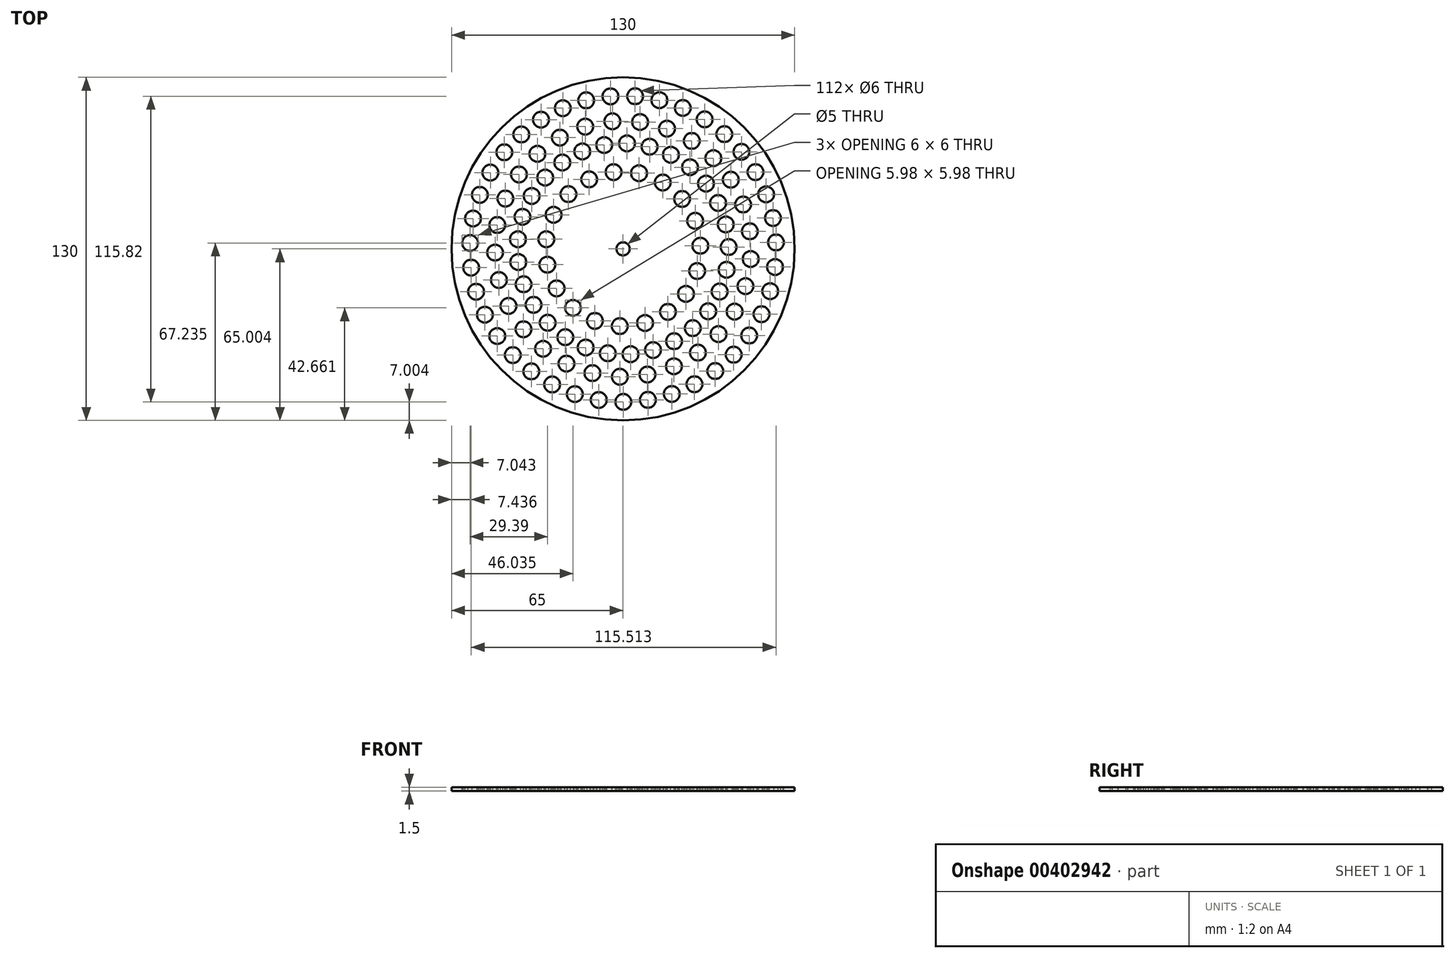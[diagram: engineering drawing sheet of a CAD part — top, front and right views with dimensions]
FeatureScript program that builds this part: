
annotation { "Feature Type Name" : "Feature", "Feature Type Description" : "" }
export const myFeature = defineFeature(function(context is Context, id is Id, definition is map)
    precondition{}
    {
        {
            var Q0;
            Q0=qCreatedBy(makeId("Top.planeOp"),FACE);
            var sketch = newSketch(context, id + "F0", { "sketchPlane" : qUnion([Q0])});
            skCircle(sketch, "E0", {"center": v(-32.16, 21.23) * mm, "radius": 65 * mm});
            skCircle(sketch, "E1", {"center": v(-32.16, 21.23) * mm, "radius": 2.5 * mm});
            skSolve(sketch);
        }
        {
            var Q0;
            Q0 = qSketchRegion(id + "F0", true);
            extrude(context, id + "F1", {"entities" : qUnion([Q0]), "flatOperationType" : FlatOperationType.REMOVE, "offsetDistance" : 25 * mm, "depth" : 1.5 * mm, "domain" : OperationDomain.MODEL});
        }
        {
            var Q0;
            Q0=makeQuery(id+"F1.opExtrude","CAP_FACE",FACE,{"disambiguationData":[OSD([sQuery(id+"F0.wireOp",EDGE,"E0")])],"isStart":false});
            var sketch = newSketch(context, id + "F2", { "sketchPlane" : qUnion([Q0])});
            skCircle(sketch, "E2", {"center": v(-90.12, 23.46) * mm, "radius": 3 * mm});
            skCircle(sketch, "E3.1.0", {"center": v(-89.72, 14.14) * mm, "radius": 3 * mm});
            skCircle(sketch, "E3.2.0", {"center": v(-87.84, 5) * mm, "radius": 3 * mm});
            skPoint(sketch, "E3.center", {"position": v(-32.16, 21.23) * mm});
            skLineSegment(sketch, "E3.anchor1", {"start": v(-32.16, 21.23) * mm, "end": v(-90.12, 23.46) * mm, "construction": true});
            skLineSegment(sketch, "E3.anchor2", {"start": v(-32.16, 21.23) * mm, "end": v(-90.12, 23.47) * mm, "construction": true});
            skCircle(sketch, "E4.1.3.0", {"center": v(-84.52, -3.72) * mm, "radius": 3 * mm});
            skCircle(sketch, "E4.1.4.0", {"center": v(-79.83, -11.8) * mm, "radius": 3 * mm});
            skCircle(sketch, "E4.1.5.0", {"center": v(-73.92, -19.02) * mm, "radius": 3 * mm});
            skCircle(sketch, "E4.1.6.0", {"center": v(-66.92, -25.2) * mm, "radius": 3 * mm});
            skCircle(sketch, "E4.1.7.0", {"center": v(-59.02, -30.17) * mm, "radius": 3 * mm});
            skCircle(sketch, "E4.1.8.0", {"center": v(-50.43, -33.81) * mm, "radius": 3 * mm});
            skCircle(sketch, "E4.1.9.0", {"center": v(-41.36, -36.03) * mm, "radius": 3 * mm});
            skCircle(sketch, "E4.1.10.0", {"center": v(-32.06, -36.77) * mm, "radius": 3 * mm});
            skCircle(sketch, "E4.1.11.0", {"center": v(-22.75, -36) * mm, "radius": 3 * mm});
            skCircle(sketch, "E4.1.12.0", {"center": v(-13.7, -33.75) * mm, "radius": 3 * mm});
            skCircle(sketch, "E4.1.13.0", {"center": v(-5.11, -30.07) * mm, "radius": 3 * mm});
            skCircle(sketch, "E4.1.14.0", {"center": v(2.77, -25.07) * mm, "radius": 3 * mm});
            skCircle(sketch, "E4.1.15.0", {"center": v(9.74, -18.87) * mm, "radius": 3 * mm});
            skCircle(sketch, "E4.1.16.0", {"center": v(15.63, -11.63) * mm, "radius": 3 * mm});
            skCircle(sketch, "E4.1.17.0", {"center": v(20.28, -3.54) * mm, "radius": 3 * mm});
            skCircle(sketch, "E4.1.18.0", {"center": v(23.58, 5.2) * mm, "radius": 3 * mm});
            skCircle(sketch, "E5.1.19.0", {"center": v(25.43, 14.35) * mm, "radius": 3 * mm});
            skCircle(sketch, "E6.1.20.0", {"center": v(25.79, 23.67) * mm, "radius": 3 * mm});
            skCircle(sketch, "E6.1.21.0", {"center": v(24.65, 32.94) * mm, "radius": 3 * mm});
            skCircle(sketch, "E6.1.22.0", {"center": v(22.03, 41.9) * mm, "radius": 3 * mm});
            skCircle(sketch, "E6.1.23.0", {"center": v(18.02, 50.32) * mm, "radius": 3 * mm});
            skCircle(sketch, "E6.1.24.0", {"center": v(12.7, 58) * mm, "radius": 3 * mm});
            skCircle(sketch, "E6.1.25.0", {"center": v(6.22, 64.72) * mm, "radius": 3 * mm});
            skCircle(sketch, "E6.1.26.0", {"center": v(-1.25, 70.31) * mm, "radius": 3 * mm});
            skCircle(sketch, "E6.1.27.0", {"center": v(-9.52, 74.63) * mm, "radius": 3 * mm});
            skCircle(sketch, "E6.1.28.0", {"center": v(-18.38, 77.57) * mm, "radius": 3 * mm});
            skCircle(sketch, "E6.1.29.0", {"center": v(-27.6, 79.05) * mm, "radius": 3 * mm});
            skCircle(sketch, "E7.1.30.0", {"center": v(-36.93, 79.04) * mm, "radius": 3 * mm});
            skCircle(sketch, "E7.1.31.0", {"center": v(-46.14, 77.52) * mm, "radius": 3 * mm});
            skCircle(sketch, "E7.1.32.0", {"center": v(-54.99, 74.55) * mm, "radius": 3 * mm});
            skCircle(sketch, "E7.1.33.0", {"center": v(-63.25, 70.2) * mm, "radius": 3 * mm});
            skCircle(sketch, "E7.1.34.0", {"center": v(-70.7, 64.58) * mm, "radius": 3 * mm});
            skCircle(sketch, "E7.1.35.0", {"center": v(-77.15, 57.83) * mm, "radius": 3 * mm});
            skCircle(sketch, "E7.1.36.0", {"center": v(-82.44, 50.14) * mm, "radius": 3 * mm});
            skCircle(sketch, "E7.1.37.0", {"center": v(-86.43, 41.7) * mm, "radius": 3 * mm});
            skCircle(sketch, "E7.1.38.0", {"center": v(-89, 32.73) * mm, "radius": 3 * mm});
            skCircle(sketch, "E7.1.39.0", {"center": v(-90.12, 23.47) * mm, "radius": 3 * mm});
            skCircle(sketch, "E8", {"center": v(-33.37, -27.25) * mm, "radius": 3 * mm});
            skCircle(sketch, "E9.1.0", {"center": v(-22.92, -26.38) * mm, "radius": 3 * mm});
            skCircle(sketch, "E9.2.0", {"center": v(-12.9, -23.28) * mm, "radius": 3 * mm});
            skLineSegment(sketch, "E9.anchor1", {"start": v(-32.16, 21.23) * mm, "end": v(-33.37, -27.25) * mm, "construction": true});
            skLineSegment(sketch, "E9.anchor2", {"start": v(-32.16, 21.23) * mm, "end": v(-33.37, -27.25) * mm, "construction": true});
            skCircle(sketch, "E10.1.3.0", {"center": v(-3.78, -18.1) * mm, "radius": 3 * mm});
            skCircle(sketch, "E10.1.4.0", {"center": v(4, -11.08) * mm, "radius": 3 * mm});
            skCircle(sketch, "E10.1.5.0", {"center": v(10.1, -2.55) * mm, "radius": 3 * mm});
            skCircle(sketch, "E10.1.6.0", {"center": v(14.23, 7.1) * mm, "radius": 3 * mm});
            skCircle(sketch, "E10.1.7.0", {"center": v(16.19, 17.4) * mm, "radius": 3 * mm});
            skCircle(sketch, "E10.1.8.0", {"center": v(15.88, 27.88) * mm, "radius": 3 * mm});
            skCircle(sketch, "E10.1.9.0", {"center": v(13.33, 38.05) * mm, "radius": 3 * mm});
            skCircle(sketch, "E10.1.10.0", {"center": v(8.65, 47.44) * mm, "radius": 3 * mm});
            skCircle(sketch, "E10.1.11.0", {"center": v(2.06, 55.6) * mm, "radius": 3 * mm});
            skCircle(sketch, "E10.1.12.0", {"center": v(-6.12, 62.15) * mm, "radius": 3 * mm});
            skCircle(sketch, "E10.1.13.0", {"center": v(-15.53, 66.8) * mm, "radius": 3 * mm});
            skCircle(sketch, "E10.1.14.0", {"center": v(-25.71, 69.3) * mm, "radius": 3 * mm});
            skCircle(sketch, "E10.1.15.0", {"center": v(-36.2, 69.57) * mm, "radius": 3 * mm});
            skCircle(sketch, "E10.1.16.0", {"center": v(-46.5, 67.57) * mm, "radius": 3 * mm});
            skCircle(sketch, "E10.1.17.0", {"center": v(-56.12, 63.4) * mm, "radius": 3 * mm});
            skCircle(sketch, "E10.1.18.0", {"center": v(-64.62, 57.27) * mm, "radius": 3 * mm});
            skCircle(sketch, "E11.1.19.0", {"center": v(-71.6, 49.45) * mm, "radius": 3 * mm});
            skCircle(sketch, "E12.1.20.0", {"center": v(-76.75, 40.3) * mm, "radius": 3 * mm});
            skCircle(sketch, "E12.1.21.0", {"center": v(-79.8, 30.27) * mm, "radius": 3 * mm});
            skCircle(sketch, "E12.1.22.0", {"center": v(-80.64, 19.82) * mm, "radius": 3 * mm});
            skCircle(sketch, "E12.1.23.0", {"center": v(-79.2, 9.43) * mm, "radius": 3 * mm});
            skCircle(sketch, "E12.1.24.0", {"center": v(-75.56, -0.4) * mm, "radius": 3 * mm});
            skCircle(sketch, "E12.1.25.0", {"center": v(-69.9, -9.23) * mm, "radius": 3 * mm});
            skCircle(sketch, "E12.1.26.0", {"center": v(-62.47, -16.63) * mm, "radius": 3 * mm});
            skCircle(sketch, "E12.1.27.0", {"center": v(-53.62, -22.26) * mm, "radius": 3 * mm});
            skCircle(sketch, "E12.1.28.0", {"center": v(-43.77, -25.86) * mm, "radius": 3 * mm});
            skCircle(sketch, "E13", {"center": v(-60.73, -6.76) * mm, "radius": 3 * mm});
            skCircle(sketch, "E14.1.0", {"center": v(-54.04, -12.25) * mm, "radius": 3 * mm});
            skCircle(sketch, "E14.2.0", {"center": v(-46.33, -16.17) * mm, "radius": 3 * mm});
            skLineSegment(sketch, "E14.anchor1", {"start": v(-32.16, 21.23) * mm, "end": v(-60.73, -6.76) * mm, "construction": true});
            skLineSegment(sketch, "E14.anchor2", {"start": v(-32.16, 21.23) * mm, "end": v(-60.73, -6.76) * mm, "construction": true});
            skCircle(sketch, "E15.1.3.0", {"center": v(-37.96, -18.34) * mm, "radius": 3 * mm});
            skCircle(sketch, "E15.1.4.0", {"center": v(-29.31, -18.67) * mm, "radius": 3 * mm});
            skCircle(sketch, "E15.1.5.0", {"center": v(-20.8, -17.12) * mm, "radius": 3 * mm});
            skCircle(sketch, "E15.1.6.0", {"center": v(-12.82, -13.78) * mm, "radius": 3 * mm});
            skCircle(sketch, "E15.1.7.0", {"center": v(-5.75, -8.8) * mm, "radius": 3 * mm});
            skCircle(sketch, "E15.1.8.0", {"center": v(0.1, -2.43) * mm, "radius": 3 * mm});
            skCircle(sketch, "E15.1.9.0", {"center": v(4.42, 5.06) * mm, "radius": 3 * mm});
            skCircle(sketch, "E15.1.10.0", {"center": v(7.05, 13.3) * mm, "radius": 3 * mm});
            skCircle(sketch, "E15.1.11.0", {"center": v(7.83, 21.91) * mm, "radius": 3 * mm});
            skCircle(sketch, "E15.1.12.0", {"center": v(6.75, 30.5) * mm, "radius": 3 * mm});
            skCircle(sketch, "E15.1.13.0", {"center": v(3.85, 38.64) * mm, "radius": 3 * mm});
            skCircle(sketch, "E15.1.14.0", {"center": v(-0.73, 45.98) * mm, "radius": 3 * mm});
            skCircle(sketch, "E15.1.15.0", {"center": v(-6.79, 52.16) * mm, "radius": 3 * mm});
            skCircle(sketch, "E15.1.16.0", {"center": v(-14.03, 56.89) * mm, "radius": 3 * mm});
            skCircle(sketch, "E15.1.17.0", {"center": v(-22.12, 59.95) * mm, "radius": 3 * mm});
            skCircle(sketch, "E15.1.18.0", {"center": v(-30.67, 61.2) * mm, "radius": 3 * mm});
            skCircle(sketch, "E16.1.19.0", {"center": v(-39.3, 60.6) * mm, "radius": 3 * mm});
            skCircle(sketch, "E17.1.20.0", {"center": v(-47.6, 58.14) * mm, "radius": 3 * mm});
            skCircle(sketch, "E17.1.21.0", {"center": v(-55.17, 53.95) * mm, "radius": 3 * mm});
            skCircle(sketch, "E17.1.22.0", {"center": v(-61.66, 48.24) * mm, "radius": 3 * mm});
            skCircle(sketch, "E17.1.23.0", {"center": v(-66.78, 41.27) * mm, "radius": 3 * mm});
            skCircle(sketch, "E17.1.24.0", {"center": v(-70.28, 33.36) * mm, "radius": 3 * mm});
            skCircle(sketch, "E17.1.25.0", {"center": v(-72, 24.88) * mm, "radius": 3 * mm});
            skCircle(sketch, "E17.1.26.0", {"center": v(-71.85, 16.23) * mm, "radius": 3 * mm});
            skCircle(sketch, "E17.1.27.0", {"center": v(-69.84, 7.82) * mm, "radius": 3 * mm});
            skCircle(sketch, "E17.1.28.0", {"center": v(-66.08, 0.03) * mm, "radius": 3 * mm});
            skCircle(sketch, "E18", {"center": v(-51.12, -1.1) * mm, "radius": 3 * mm});
            skCircle(sketch, "E19.1.0", {"center": v(-42.84, -6.06) * mm, "radius": 3 * mm});
            skCircle(sketch, "E19.2.0", {"center": v(-33.4, -8.05) * mm, "radius": 3 * mm});
            skLineSegment(sketch, "E19.anchor1", {"start": v(-32.16, 21.23) * mm, "end": v(-51.12, -1.1) * mm, "construction": true});
            skLineSegment(sketch, "E19.anchor2", {"start": v(-32.16, 21.23) * mm, "end": v(-51.12, -1.1) * mm, "construction": true});
            skCircle(sketch, "E20.1.3.0", {"center": v(-23.83, -6.86) * mm, "radius": 3 * mm});
            skCircle(sketch, "E20.1.4.0", {"center": v(-15.16, -2.64) * mm, "radius": 3 * mm});
            skCircle(sketch, "E20.1.5.0", {"center": v(-8.33, 4.18) * mm, "radius": 3 * mm});
            skCircle(sketch, "E20.1.6.0", {"center": v(-4.08, 12.84) * mm, "radius": 3 * mm});
            skCircle(sketch, "E20.1.7.0", {"center": v(-2.88, 22.41) * mm, "radius": 3 * mm});
            skCircle(sketch, "E20.1.8.0", {"center": v(-4.85, 31.86) * mm, "radius": 3 * mm});
            skCircle(sketch, "E20.1.9.0", {"center": v(-9.78, 40.15) * mm, "radius": 3 * mm});
            skCircle(sketch, "E20.1.10.0", {"center": v(-17.13, 46.4) * mm, "radius": 3 * mm});
            skCircle(sketch, "E20.1.11.0", {"center": v(-26.11, 49.91) * mm, "radius": 3 * mm});
            skCircle(sketch, "E20.1.12.0", {"center": v(-35.75, 50.32) * mm, "radius": 3 * mm});
            skCircle(sketch, "E20.1.13.0", {"center": v(-45, 47.58) * mm, "radius": 3 * mm});
            skCircle(sketch, "E20.1.14.0", {"center": v(-52.86, 41.98) * mm, "radius": 3 * mm});
            skCircle(sketch, "E20.1.15.0", {"center": v(-58.47, 34.13) * mm, "radius": 3 * mm});
            skCircle(sketch, "E20.1.16.0", {"center": v(-61.24, 24.9) * mm, "radius": 3 * mm});
            skCircle(sketch, "E20.1.17.0", {"center": v(-60.85, 15.25) * mm, "radius": 3 * mm});
            skCircle(sketch, "E20.1.18.0", {"center": v(-57.35, 6.26) * mm, "radius": 3 * mm});
            skSolve(sketch);
        }
        {
            var Q0;
            Q0 = qSketchRegion(id + "F2", true);
            extrude(context, id + "F3", {"entities" : qUnion([Q0]), "operationType" : NewBodyOperationType.REMOVE, "depth" : -3 * mm});
        }
    });
